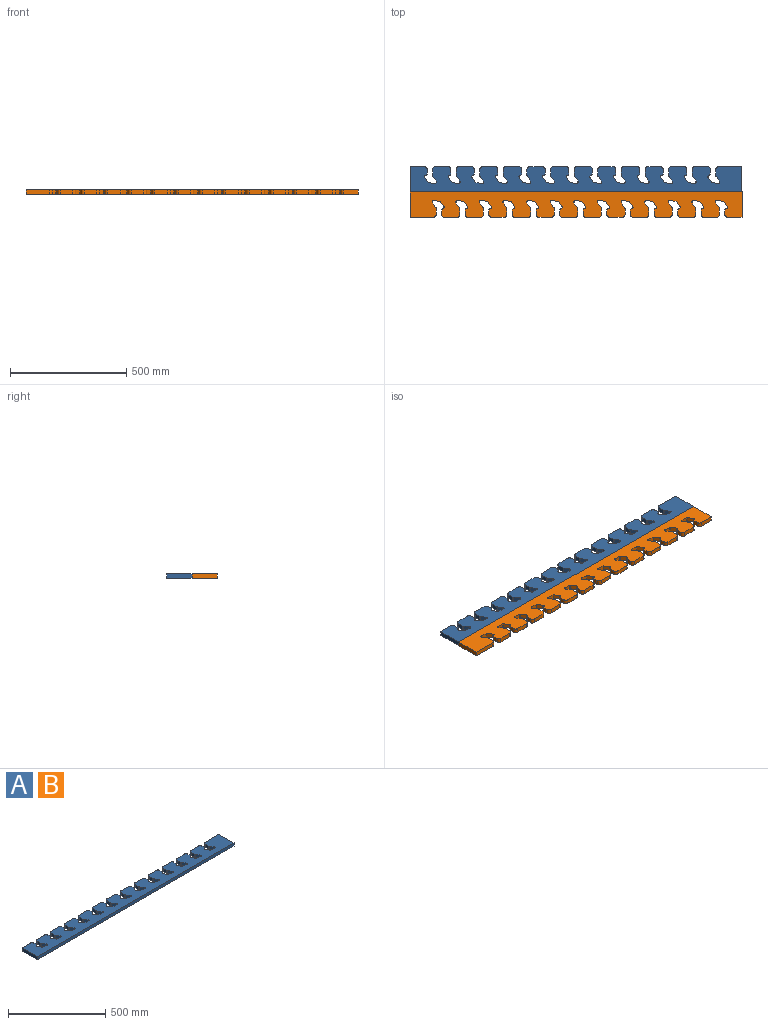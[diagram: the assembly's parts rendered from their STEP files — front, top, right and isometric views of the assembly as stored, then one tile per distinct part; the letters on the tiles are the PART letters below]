
ASSEMBLY  parts=2 mates=1
PART A: 203 faces, bbox 1428.8x109.2x19.1 mm
  f0: plane 60.96x19.05mm, normal (0,1,0), area 1161.2mm2, adj f1,f200,f201,f202
  f1: plane 109.22x19.05mm, normal (-1,0,0), area 2080.6mm2, adj f0,f2,f201,f202
  f2: plane 1428.75x19.05mm, normal (0,-1,0), area 27217.7mm2, adj f1,f3,f201,f202
  f3: plane 109.22x19.05mm, normal (1,0,0), area 2080.6mm2, adj f2,f4,f201,f202
  f4: plane 99.88x19.05mm, normal (0,1,0), area 1902.7mm2, adj f3,f5,f201,f202
  f5: cylinder r=12.7mm len=19.05mm, axis (0,0,-1), area 380mm2, adj f4,f6,f201,f202
  f6: plane 25.53x19.05mm, normal (-1,0,0), area 486.4mm2, adj f5,f7,f201,f202
  f7: cylinder r=5.08mm len=19.05mm, axis (0,0,-1), area 70mm2, adj f6,f8,f201,f202
  f8: cylinder r=6.35mm len=19.05mm, axis (0,0,-1), area 12.4mm2, adj f7,f9,f201,f202
  f9: plane 20.02x19.05mm, normal (-0.81,-0.58,0), area 468.9mm2, adj f8,f10,f201,f202
  f10: cylinder r=6.35mm len=19.05mm, axis (0,0,-1), area 277mm2, adj f9,f11,f201,f202
  f11: plane 26.38x19.05mm, normal (0.1,1,0), area 504.9mm2, adj f10,f12,f201,f202
  f12: cylinder r=2.19mm len=19.05mm, axis (0,0,-1), area 35.6mm2, adj f11,f13,f201,f202
  f13: plane 21.55x19.05mm, normal (0.81,0.58,0), area 504.9mm2, adj f12,f14,f201,f202
  f14: cylinder r=6.35mm len=19.05mm, axis (0,0,-1), area 277mm2, adj f13,f15,f201,f202
  f15: plane 19.05x1.53mm, normal (0.1,1,0), area 29.2mm2, adj f14,f16,f201,f202
  f16: cylinder r=5.08mm len=19.05mm, axis (0,0,-1), area 161.5mm2, adj f15,f17,f201,f202
  f17: plane 19.18x19.05mm, normal (1,0,0), area 365.3mm2, adj f16,f18,f201,f202
  f18: cylinder r=12.7mm len=19.05mm, axis (0,0,-1), area 380mm2, adj f17,f19,f201,f202
  f19: plane 52.88x19.05mm, normal (0,1,0), area 1007.4mm2, adj f18,f20,f201,f202
  f20: cylinder r=12.7mm len=19.05mm, axis (0,0,-1), area 380mm2, adj f19,f21,f201,f202
  f21: plane 25.53x19.05mm, normal (-1,0,0), area 486.4mm2, adj f20,f22,f201,f202
  f22: cylinder r=5.08mm len=19.05mm, axis (0,0,-1), area 70mm2, adj f21,f23,f201,f202
  f23: cylinder r=6.35mm len=19.05mm, axis (0,0,-1), area 12.4mm2, adj f22,f24,f201,f202
  f24: plane 20.02x19.05mm, normal (-0.81,-0.58,0), area 468.9mm2, adj f23,f25,f201,f202
  f25: cylinder r=6.35mm len=19.05mm, axis (0,0,-1), area 277mm2, adj f24,f26,f201,f202
  f26: plane 26.38x19.05mm, normal (0.1,1,0), area 504.9mm2, adj f25,f27,f201,f202
  f27: cylinder r=2.19mm len=19.05mm, axis (0,0,-1), area 35.6mm2, adj f26,f28,f201,f202
  f28: plane 21.55x19.05mm, normal (0.81,0.58,0), area 504.9mm2, adj f27,f29,f201,f202
  f29: cylinder r=6.35mm len=19.05mm, axis (0,0,-1), area 277mm2, adj f28,f30,f201,f202
  f30: plane 19.05x1.53mm, normal (0.1,1,0), area 29.2mm2, adj f29,f31,f201,f202
  f31: cylinder r=5.08mm len=19.05mm, axis (0,0,-1), area 161.5mm2, adj f30,f32,f201,f202
  f32: plane 19.18x19.05mm, normal (1,0,0), area 365.3mm2, adj f31,f33,f201,f202
  f33: cylinder r=12.7mm len=19.05mm, axis (0,0,-1), area 380mm2, adj f32,f34,f201,f202
  f34: plane 52.88x19.05mm, normal (0,1,0), area 1007.4mm2, adj f33,f35,f201,f202
  f35: cylinder r=12.7mm len=19.05mm, axis (0,0,-1), area 380mm2, adj f34,f36,f201,f202
  f36: plane 25.53x19.05mm, normal (-1,0,0), area 486.4mm2, adj f35,f37,f201,f202
  f37: cylinder r=5.08mm len=19.05mm, axis (0,0,-1), area 70mm2, adj f36,f38,f201,f202
  f38: cylinder r=6.35mm len=19.05mm, axis (0,0,-1), area 12.4mm2, adj f37,f39,f201,f202
  f39: plane 20.02x19.05mm, normal (-0.81,-0.58,0), area 468.9mm2, adj f38,f40,f201,f202
  f40: cylinder r=6.35mm len=19.05mm, axis (0,0,-1), area 277mm2, adj f39,f41,f201,f202
  f41: plane 26.38x19.05mm, normal (0.1,1,0), area 504.9mm2, adj f40,f42,f201,f202
  f42: cylinder r=2.19mm len=19.05mm, axis (0,0,-1), area 35.6mm2, adj f41,f43,f201,f202
  f43: plane 21.55x19.05mm, normal (0.81,0.58,0), area 504.9mm2, adj f42,f44,f201,f202
  f44: cylinder r=6.35mm len=19.05mm, axis (0,0,-1), area 277mm2, adj f43,f45,f201,f202
  f45: plane 19.05x1.53mm, normal (0.1,1,0), area 29.2mm2, adj f44,f46,f201,f202
  f46: cylinder r=5.08mm len=19.05mm, axis (0,0,-1), area 161.5mm2, adj f45,f47,f201,f202
  f47: plane 19.18x19.05mm, normal (1,0,0), area 365.3mm2, adj f46,f48,f201,f202
  f48: cylinder r=12.7mm len=19.05mm, axis (0,0,-1), area 380mm2, adj f47,f49,f201,f202
  f49: plane 52.88x19.05mm, normal (0,1,0), area 1007.4mm2, adj f48,f50,f201,f202
  f50: cylinder r=12.7mm len=19.05mm, axis (0,0,-1), area 380mm2, adj f49,f51,f201,f202
  f51: plane 25.53x19.05mm, normal (-1,0,0), area 486.4mm2, adj f50,f52,f201,f202
  f52: cylinder r=5.08mm len=19.05mm, axis (0,0,-1), area 70mm2, adj f51,f53,f201,f202
  f53: cylinder r=6.35mm len=19.05mm, axis (0,0,-1), area 12.4mm2, adj f52,f54,f201,f202
  f54: plane 20.02x19.05mm, normal (-0.81,-0.58,0), area 468.9mm2, adj f53,f55,f201,f202
  f55: cylinder r=6.35mm len=19.05mm, axis (0,0,-1), area 277mm2, adj f54,f56,f201,f202
  f56: plane 26.38x19.05mm, normal (0.1,1,0), area 504.9mm2, adj f55,f57,f201,f202
  f57: cylinder r=2.19mm len=19.05mm, axis (0,0,-1), area 35.6mm2, adj f56,f58,f201,f202
  f58: plane 21.55x19.05mm, normal (0.81,0.58,0), area 504.9mm2, adj f57,f59,f201,f202
  f59: cylinder r=6.35mm len=19.05mm, axis (0,0,-1), area 277mm2, adj f58,f60,f201,f202
  f60: plane 19.05x1.53mm, normal (0.1,1,0), area 29.2mm2, adj f59,f61,f201,f202
  f61: cylinder r=5.08mm len=19.05mm, axis (0,0,-1), area 161.5mm2, adj f60,f62,f201,f202
  f62: plane 19.18x19.05mm, normal (1,0,0), area 365.3mm2, adj f61,f63,f201,f202
  f63: cylinder r=12.7mm len=19.05mm, axis (0,0,-1), area 380mm2, adj f62,f64,f201,f202
  f64: plane 52.88x19.05mm, normal (0,1,0), area 1007.4mm2, adj f63,f65,f201,f202
  f65: cylinder r=12.7mm len=19.05mm, axis (0,0,-1), area 380mm2, adj f64,f66,f201,f202
  f66: plane 25.53x19.05mm, normal (-1,0,0), area 486.4mm2, adj f65,f67,f201,f202
  f67: cylinder r=5.08mm len=19.05mm, axis (0,0,-1), area 70mm2, adj f66,f68,f201,f202
  f68: cylinder r=6.35mm len=19.05mm, axis (0,0,-1), area 12.4mm2, adj f67,f69,f201,f202
  f69: plane 20.02x19.05mm, normal (-0.81,-0.58,0), area 468.9mm2, adj f68,f70,f201,f202
  f70: cylinder r=6.35mm len=19.05mm, axis (0,0,-1), area 277mm2, adj f69,f71,f201,f202
  f71: plane 26.38x19.05mm, normal (0.1,1,0), area 504.9mm2, adj f70,f72,f201,f202
  f72: cylinder r=2.19mm len=19.05mm, axis (0,0,-1), area 35.6mm2, adj f71,f73,f201,f202
  f73: plane 21.55x19.05mm, normal (0.81,0.58,0), area 504.9mm2, adj f72,f74,f201,f202
  f74: cylinder r=6.35mm len=19.05mm, axis (0,0,-1), area 277mm2, adj f73,f75,f201,f202
  f75: plane 19.05x1.53mm, normal (0.1,1,0), area 29.2mm2, adj f74,f76,f201,f202
  f76: cylinder r=5.08mm len=19.05mm, axis (0,0,-1), area 161.5mm2, adj f75,f77,f201,f202
  f77: plane 19.18x19.05mm, normal (1,0,0), area 365.3mm2, adj f76,f78,f201,f202
  f78: cylinder r=12.7mm len=19.05mm, axis (0,0,-1), area 380mm2, adj f77,f79,f201,f202
  f79: plane 52.88x19.05mm, normal (0,1,0), area 1007.4mm2, adj f78,f80,f201,f202
  f80: cylinder r=12.7mm len=19.05mm, axis (0,0,-1), area 380mm2, adj f79,f81,f201,f202
  f81: plane 25.53x19.05mm, normal (-1,0,0), area 486.4mm2, adj f80,f82,f201,f202
  f82: cylinder r=5.08mm len=19.05mm, axis (0,0,-1), area 70mm2, adj f81,f83,f201,f202
  f83: cylinder r=6.35mm len=19.05mm, axis (0,0,-1), area 12.4mm2, adj f82,f84,f201,f202
  f84: plane 20.02x19.05mm, normal (-0.81,-0.58,0), area 468.9mm2, adj f83,f85,f201,f202
  f85: cylinder r=6.35mm len=19.05mm, axis (0,0,-1), area 277mm2, adj f84,f86,f201,f202
  f86: plane 26.38x19.05mm, normal (0.1,1,0), area 504.9mm2, adj f85,f87,f201,f202
  f87: cylinder r=2.19mm len=19.05mm, axis (0,0,-1), area 35.6mm2, adj f86,f88,f201,f202
  f88: plane 21.55x19.05mm, normal (0.81,0.58,0), area 504.9mm2, adj f87,f89,f201,f202
  f89: cylinder r=6.35mm len=19.05mm, axis (0,0,-1), area 277mm2, adj f88,f90,f201,f202
  f90: plane 19.05x1.53mm, normal (0.1,1,0), area 29.2mm2, adj f89,f91,f201,f202
  f91: cylinder r=5.08mm len=19.05mm, axis (0,0,-1), area 161.5mm2, adj f90,f92,f201,f202
  f92: plane 19.18x19.05mm, normal (1,0,0), area 365.3mm2, adj f91,f93,f201,f202
  f93: cylinder r=12.7mm len=19.05mm, axis (0,0,-1), area 380mm2, adj f92,f94,f201,f202
  f94: plane 52.88x19.05mm, normal (0,1,0), area 1007.4mm2, adj f93,f95,f201,f202
  f95: cylinder r=12.7mm len=19.05mm, axis (0,0,-1), area 380mm2, adj f94,f96,f201,f202
  f96: plane 25.53x19.05mm, normal (-1,0,0), area 486.4mm2, adj f95,f97,f201,f202
  f97: cylinder r=5.08mm len=19.05mm, axis (0,0,-1), area 70mm2, adj f96,f98,f201,f202
  f98: cylinder r=6.35mm len=19.05mm, axis (0,0,-1), area 12.4mm2, adj f97,f99,f201,f202
  f99: plane 20.02x19.05mm, normal (-0.81,-0.58,0), area 468.9mm2, adj f98,f100,f201,f202
  f100: cylinder r=6.35mm len=19.05mm, axis (0,0,-1), area 277mm2, adj f99,f101,f201,f202
  f101: plane 26.38x19.05mm, normal (0.1,1,0), area 504.9mm2, adj f100,f102,f201,f202
  f102: cylinder r=2.19mm len=19.05mm, axis (0,0,-1), area 35.6mm2, adj f101,f103,f201,f202
  f103: plane 21.55x19.05mm, normal (0.81,0.58,0), area 504.9mm2, adj f102,f104,f201,f202
  f104: cylinder r=6.35mm len=19.05mm, axis (0,0,-1), area 277mm2, adj f103,f105,f201,f202
  f105: plane 19.05x1.53mm, normal (0.1,1,0), area 29.2mm2, adj f104,f106,f201,f202
  f106: cylinder r=5.08mm len=19.05mm, axis (0,0,-1), area 161.5mm2, adj f105,f107,f201,f202
  f107: plane 19.18x19.05mm, normal (1,0,0), area 365.3mm2, adj f106,f108,f201,f202
  f108: extruded ~19.05x7.08mm, area 141.2mm2, adj f107,f109,f201,f202
  f109: cylinder r=12.7mm len=19.05mm, axis (0,0,-1), area 229.2mm2, adj f108,f110,f201,f202
  f110: extruded ~19.05x0.41mm, area 7.7mm2, adj f109,f111,f201,f202
  f111: plane 52.88x19.05mm, normal (0,1,0), area 1007.4mm2, adj f110,f112,f201,f202
  f112: cylinder r=12.7mm len=19.05mm, axis (0,0,-1), area 380mm2, adj f111,f113,f201,f202
  f113: plane 25.53x19.05mm, normal (-1,0,0), area 486.4mm2, adj f112,f114,f201,f202
  f114: cylinder r=5.08mm len=19.05mm, axis (0,0,-1), area 70mm2, adj f113,f115,f201,f202
  f115: cylinder r=6.35mm len=19.05mm, axis (0,0,-1), area 12.4mm2, adj f114,f116,f201,f202
  f116: plane 20.02x19.05mm, normal (-0.81,-0.58,0), area 468.9mm2, adj f115,f117,f201,f202
  f117: cylinder r=6.35mm len=19.05mm, axis (0,0,-1), area 277mm2, adj f116,f118,f201,f202
  f118: plane 26.38x19.05mm, normal (0.1,1,0), area 504.9mm2, adj f117,f119,f201,f202
  f119: cylinder r=2.19mm len=19.05mm, axis (0,0,-1), area 35.6mm2, adj f118,f120,f201,f202
  f120: plane 21.55x19.05mm, normal (0.81,0.58,0), area 504.9mm2, adj f119,f121,f201,f202
  f121: cylinder r=6.35mm len=19.05mm, axis (0,0,-1), area 277mm2, adj f120,f122,f201,f202
  f122: plane 19.05x1.53mm, normal (0.1,1,0), area 29.2mm2, adj f121,f123,f201,f202
  f123: cylinder r=5.08mm len=19.05mm, axis (0,0,-1), area 161.5mm2, adj f122,f124,f201,f202
  f124: plane 19.18x19.05mm, normal (1,0,0), area 365.3mm2, adj f123,f125,f201,f202
  f125: cylinder r=12.7mm len=19.05mm, axis (0,0,-1), area 380mm2, adj f124,f126,f201,f202
  f126: plane 52.88x19.05mm, normal (0,1,0), area 1007.4mm2, adj f125,f127,f201,f202
  f127: cylinder r=12.7mm len=19.05mm, axis (0,0,-1), area 380mm2, adj f126,f128,f201,f202
  f128: plane 25.53x19.05mm, normal (-1,0,0), area 486.4mm2, adj f127,f129,f201,f202
  f129: cylinder r=5.08mm len=19.05mm, axis (0,0,-1), area 70mm2, adj f128,f130,f201,f202
  f130: cylinder r=6.35mm len=19.05mm, axis (0,0,-1), area 12.4mm2, adj f129,f131,f201,f202
  f131: plane 20.02x19.05mm, normal (-0.81,-0.58,0), area 468.9mm2, adj f130,f132,f201,f202
  f132: cylinder r=6.35mm len=19.05mm, axis (0,0,-1), area 277mm2, adj f131,f133,f201,f202
  f133: plane 26.38x19.05mm, normal (0.1,1,0), area 504.9mm2, adj f132,f134,f201,f202
  f134: cylinder r=2.19mm len=19.05mm, axis (0,0,-1), area 35.6mm2, adj f133,f135,f201,f202
  f135: plane 21.55x19.05mm, normal (0.81,0.58,0), area 504.9mm2, adj f134,f136,f201,f202
  f136: cylinder r=6.35mm len=19.05mm, axis (0,0,-1), area 277mm2, adj f135,f137,f201,f202
  f137: plane 19.05x1.53mm, normal (0.1,1,0), area 29.2mm2, adj f136,f138,f201,f202
  f138: cylinder r=5.08mm len=19.05mm, axis (0,0,-1), area 161.5mm2, adj f137,f139,f201,f202
  f139: plane 19.18x19.05mm, normal (1,0,0), area 365.3mm2, adj f138,f140,f201,f202
  f140: cylinder r=12.7mm len=19.05mm, axis (0,0,-1), area 380mm2, adj f139,f141,f201,f202
  f141: plane 52.88x19.05mm, normal (0,1,0), area 1007.4mm2, adj f140,f142,f201,f202
  f142: cylinder r=12.7mm len=19.05mm, axis (0,0,-1), area 380mm2, adj f141,f143,f201,f202
  f143: plane 25.53x19.05mm, normal (-1,0,0), area 486.4mm2, adj f142,f144,f201,f202
  f144: cylinder r=5.08mm len=19.05mm, axis (0,0,-1), area 70mm2, adj f143,f145,f201,f202
  f145: cylinder r=6.35mm len=19.05mm, axis (0,0,-1), area 12.4mm2, adj f144,f146,f201,f202
  f146: plane 20.02x19.05mm, normal (-0.81,-0.58,0), area 468.9mm2, adj f145,f147,f201,f202
  f147: cylinder r=6.35mm len=19.05mm, axis (0,0,-1), area 277mm2, adj f146,f148,f201,f202
  f148: plane 26.38x19.05mm, normal (0.1,1,0), area 504.9mm2, adj f147,f149,f201,f202
  f149: cylinder r=2.19mm len=19.05mm, axis (0,0,-1), area 35.6mm2, adj f148,f150,f201,f202
  f150: plane 21.55x19.05mm, normal (0.81,0.58,0), area 504.9mm2, adj f149,f151,f201,f202
  f151: cylinder r=6.35mm len=19.05mm, axis (0,0,-1), area 277mm2, adj f150,f152,f201,f202
  f152: plane 19.05x1.53mm, normal (0.1,1,0), area 29.2mm2, adj f151,f153,f201,f202
  f153: cylinder r=5.08mm len=19.05mm, axis (0,0,-1), area 161.5mm2, adj f152,f154,f201,f202
  f154: plane 19.18x19.05mm, normal (1,0,0), area 365.3mm2, adj f153,f155,f201,f202
  f155: cylinder r=12.7mm len=19.05mm, axis (0,0,-1), area 380mm2, adj f154,f156,f201,f202
  f156: plane 52.88x19.05mm, normal (0,1,0), area 1007.4mm2, adj f155,f157,f201,f202
  f157: cylinder r=12.7mm len=19.05mm, axis (0,0,-1), area 380mm2, adj f156,f158,f201,f202
  f158: plane 25.53x19.05mm, normal (-1,0,0), area 486.4mm2, adj f157,f159,f201,f202
  f159: cylinder r=5.08mm len=19.05mm, axis (0,0,-1), area 70mm2, adj f158,f160,f201,f202
  f160: cylinder r=6.35mm len=19.05mm, axis (0,0,-1), area 12.4mm2, adj f159,f161,f201,f202
  f161: plane 20.02x19.05mm, normal (-0.81,-0.58,0), area 468.9mm2, adj f160,f162,f201,f202
  f162: cylinder r=6.35mm len=19.05mm, axis (0,0,-1), area 277mm2, adj f161,f163,f201,f202
  f163: plane 26.38x19.05mm, normal (0.1,1,0), area 504.9mm2, adj f162,f164,f201,f202
  f164: cylinder r=2.19mm len=19.05mm, axis (0,0,-1), area 35.6mm2, adj f163,f165,f201,f202
  f165: plane 21.55x19.05mm, normal (0.81,0.58,0), area 504.9mm2, adj f164,f166,f201,f202
  f166: cylinder r=6.35mm len=19.05mm, axis (0,0,-1), area 277mm2, adj f165,f167,f201,f202
  f167: plane 19.05x1.53mm, normal (0.1,1,0), area 29.2mm2, adj f166,f168,f201,f202
  f168: cylinder r=5.08mm len=19.05mm, axis (0,0,-1), area 161.5mm2, adj f167,f169,f201,f202
  f169: plane 19.18x19.05mm, normal (1,0,0), area 365.3mm2, adj f168,f170,f201,f202
  f170: cylinder r=12.7mm len=19.05mm, axis (0,0,-1), area 380mm2, adj f169,f171,f201,f202
  f171: plane 52.88x19.05mm, normal (0,1,0), area 1007.4mm2, adj f170,f172,f201,f202
  f172: cylinder r=12.7mm len=19.05mm, axis (0,0,-1), area 380mm2, adj f171,f173,f201,f202
  f173: plane 25.53x19.05mm, normal (-1,0,0), area 486.4mm2, adj f172,f174,f201,f202
  f174: cylinder r=5.08mm len=19.05mm, axis (0,0,-1), area 70mm2, adj f173,f175,f201,f202
  f175: cylinder r=6.35mm len=19.05mm, axis (0,0,-1), area 12.4mm2, adj f174,f176,f201,f202
  f176: plane 20.02x19.05mm, normal (-0.81,-0.58,0), area 468.9mm2, adj f175,f177,f201,f202
  f177: cylinder r=6.35mm len=19.05mm, axis (0,0,-1), area 277mm2, adj f176,f178,f201,f202
  f178: plane 26.38x19.05mm, normal (0.1,1,0), area 504.9mm2, adj f177,f179,f201,f202
  f179: cylinder r=2.19mm len=19.05mm, axis (0,0,-1), area 35.6mm2, adj f178,f180,f201,f202
  f180: plane 21.55x19.05mm, normal (0.81,0.58,0), area 504.9mm2, adj f179,f181,f201,f202
  f181: cylinder r=6.35mm len=19.05mm, axis (0,0,-1), area 277mm2, adj f180,f182,f201,f202
  f182: plane 19.05x1.53mm, normal (0.1,1,0), area 29.2mm2, adj f181,f183,f201,f202
  f183: cylinder r=5.08mm len=19.05mm, axis (0,0,-1), area 161.5mm2, adj f182,f184,f201,f202
  f184: plane 19.18x19.05mm, normal (1,0,0), area 365.3mm2, adj f183,f185,f201,f202
  f185: cylinder r=12.7mm len=19.05mm, axis (0,0,-1), area 380mm2, adj f184,f186,f201,f202
  f186: plane 52.88x19.05mm, normal (0,1,0), area 1007.4mm2, adj f185,f187,f201,f202
  f187: cylinder r=12.7mm len=19.05mm, axis (0,0,-1), area 380mm2, adj f186,f188,f201,f202
  f188: plane 25.53x19.05mm, normal (-1,0,0), area 486.4mm2, adj f187,f189,f201,f202
  f189: cylinder r=5.08mm len=19.05mm, axis (0,0,-1), area 70mm2, adj f188,f190,f201,f202
  f190: cylinder r=6.35mm len=19.05mm, axis (0,0,-1), area 12.4mm2, adj f189,f191,f201,f202
  f191: plane 20.02x19.05mm, normal (-0.81,-0.58,0), area 468.9mm2, adj f190,f192,f201,f202
  f192: cylinder r=6.35mm len=19.05mm, axis (0,0,-1), area 277mm2, adj f191,f193,f201,f202
  f193: plane 26.38x19.05mm, normal (0.1,1,0), area 504.9mm2, adj f192,f194,f201,f202
  f194: cylinder r=2.19mm len=19.05mm, axis (0,0,-1), area 35.6mm2, adj f193,f195,f201,f202
  f195: plane 21.55x19.05mm, normal (0.81,0.58,0), area 504.9mm2, adj f194,f196,f201,f202
  f196: cylinder r=6.35mm len=19.05mm, axis (0,0,-1), area 277mm2, adj f195,f197,f201,f202
  f197: plane 19.05x1.53mm, normal (0.1,1,0), area 29.2mm2, adj f196,f198,f201,f202
  f198: cylinder r=5.08mm len=19.05mm, axis (0,0,-1), area 161.5mm2, adj f197,f199,f201,f202
  f199: plane 19.18x19.05mm, normal (1,0,0), area 365.3mm2, adj f198,f200,f201,f202
  f200: cylinder r=12.7mm len=19.05mm, axis (0,0,-1), area 380mm2, adj f0,f199,f201,f202
  f201: plane 1428.75x109.22mm, normal (0,0,1), area 127617.5mm2, adj f0,f1,f2,f3,f4,f5,f6,f7
  f202: plane 1428.75x109.22mm, normal (0,0,-1), area 127617.5mm2, adj f0,f1,f2,f3,f4,f5,f6,f7
PART B: same geometry as A
PLACE A t=(-1072,96.61,-94.04)mm
PLACE B rot(axis=(0,0,-1),180deg) t=(356.75,96.61,-94.04)mm
MATE planar A.f2 <-> B.f2  axis (0,-1,0) through (356.75,96.61,-84.51)mm
